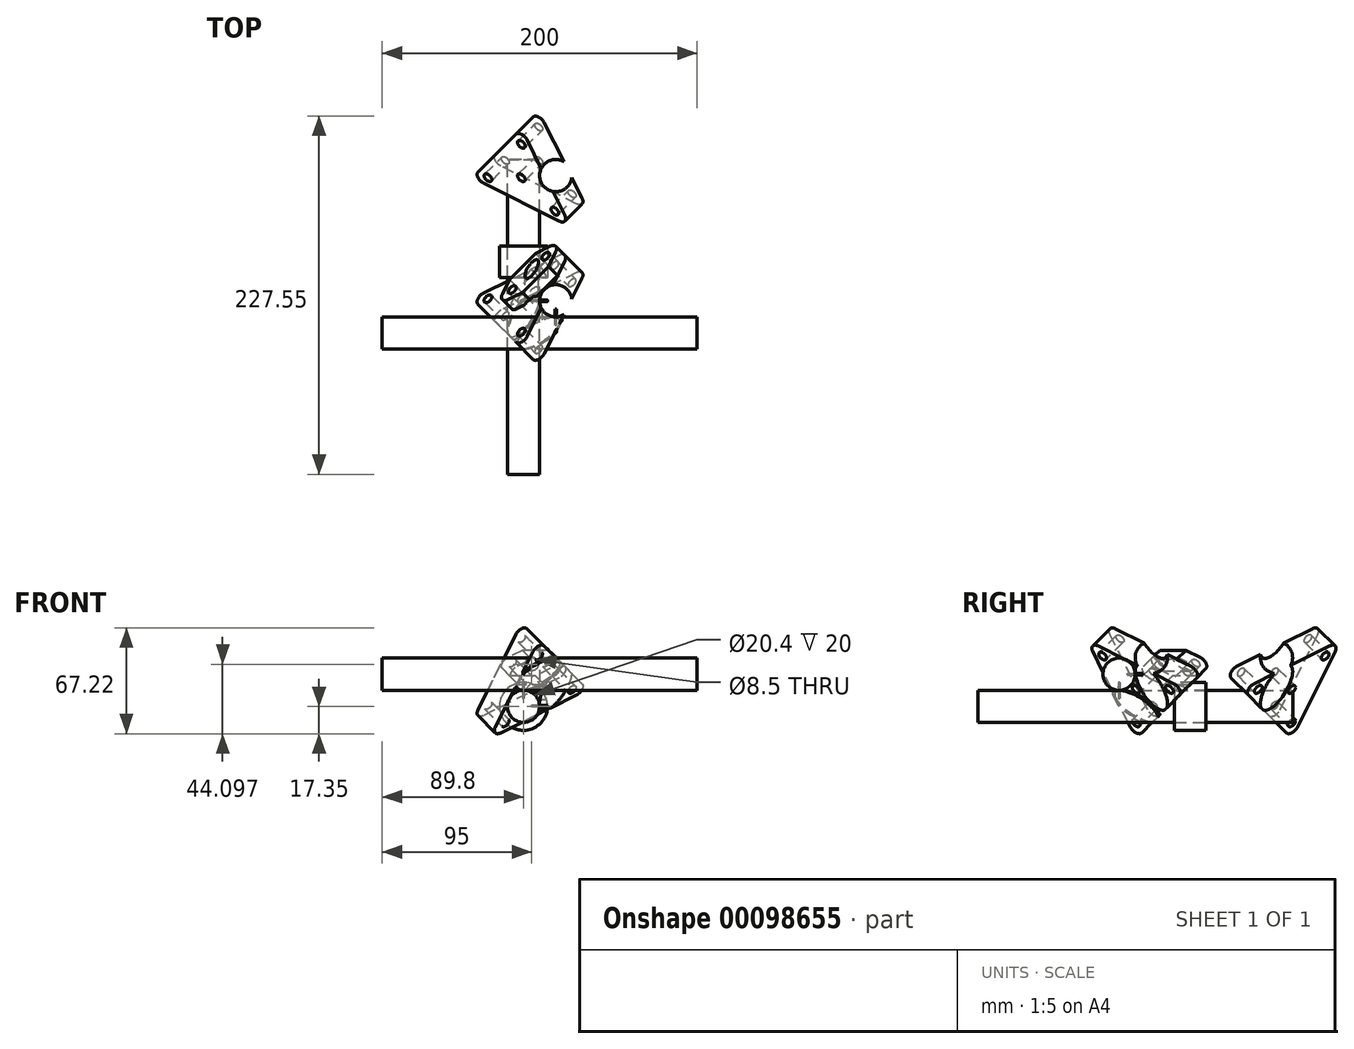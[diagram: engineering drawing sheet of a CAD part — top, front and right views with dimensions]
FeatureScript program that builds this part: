
annotation { "Feature Type Name" : "Feature", "Feature Type Description" : "" }
export const myFeature = defineFeature(function(context is Context, id is Id, definition is map)
    precondition{}
    {
        {
            var Q0;
            Q0=qCreatedBy(makeId("Top.planeOp"),FACE);
            var sketch = newSketch(context, id + "F0", { "sketchPlane" : qUnion([Q0])});
            skCircle(sketch, "E0", {"center": v(10.25, 10.25) * mm, "radius": 10.25 * mm});
            skLineSegment(sketch, "E1", {"start": v(3, 3) * mm, "end": v(14.79, -8.78) * mm, "construction": true});
            skLineSegment(sketch, "E2", {"start": v(30.79, 4.2) * mm, "end": v(17.5, 17.5) * mm, "construction": true});
            skLineSegment(sketch, "E3", {"start": v(0, 0) * mm, "end": v(17.5, 17.5) * mm, "construction": true});
            skLineSegment(sketch, "E4", {"start": v(14.79, -8.78) * mm, "end": v(30.79, 4.2) * mm, "construction": true});
            skSolve(sketch);
        }
        {
            var Q0;
            Q0=qSketchRegion(id+"F0",true);
            extrude(context, id + "F1", {"entities" : qUnion([Q0]), "endBound" : BoundingType.SYMMETRIC, "depth" : 200 * mm});
        }
        {
            var Q0;
            Q0=qCreatedBy(makeId("Right.planeOp"),FACE);
            var sketch = newSketch(context, id + "F2", { "sketchPlane" : qUnion([Q0])});
            skCircle(sketch, "E5", {"center": v(-10.25, 10.25) * mm, "radius": 10.25 * mm});
            skLineSegment(sketch, "E6", {"start": v(0, 0) * mm, "end": v(-17.5, 17.5) * mm, "construction": true});
            skLineSegment(sketch, "E7", {"start": v(-3, 3) * mm, "end": v(-20.36, -14.35) * mm, "construction": true});
            skLineSegment(sketch, "E8", {"start": v(-20.36, -14.35) * mm, "end": v(-34.85, 0.14) * mm, "construction": true});
            skLineSegment(sketch, "E9", {"start": v(-34.85, 0.14) * mm, "end": v(-17.5, 17.5) * mm, "construction": true});
            skSolve(sketch);
        }
        {
            var Q0;
            Q0=qSketchRegion(id+"F2",true);
            extrude(context, id + "F3", {"entities" : qUnion([Q0]), "endBound" : BoundingType.SYMMETRIC, "depth" : 200 * mm});
        }
        {
            var Q0;
            Q0=qCreatedBy(makeId("Front.planeOp"),FACE);
            var sketch = newSketch(context, id + "F4", { "sketchPlane" : qUnion([Q0])});
            skCircle(sketch, "E10", {"center": v(-10.2, -10.2) * mm, "radius": 10.2 * mm});
            skLineSegment(sketch, "E11", {"start": v(0, 0) * mm, "end": v(-17.41, -17.41) * mm, "construction": true});
            skLineSegment(sketch, "E12", {"start": v(-2.99, -2.99) * mm, "end": v(15.73, -21.7) * mm, "construction": true});
            skLineSegment(sketch, "E13", {"start": v(15.73, -21.7) * mm, "end": v(1.3, -36.13) * mm, "construction": true});
            skLineSegment(sketch, "E14", {"start": v(1.3, -36.13) * mm, "end": v(-17.41, -17.41) * mm, "construction": true});
            skSolve(sketch);
        }
        {
            var Q0;
            Q0=qSketchRegion(id+"F4",true);
            extrude(context, id + "F5", {"entities" : qUnion([Q0]), "endBound" : BoundingType.SYMMETRIC, "depth" : 200 * mm});
        }
        {
            var Q0;
            Q0=sQuery(id+"F2.wireOp",VERTEX,"E5.center");
            var Q1;
            Q1=sQuery(id+"F4.wireOp",VERTEX,"E10.center");
            var Q2;
            Q2=sQuery(id+"F0.wireOp",VERTEX,"E0.center");
            cPlane(context, id + "F6", {"entities" : qUnion([Q0, Q1, Q2]), "cplaneType" : CPlaneType.THREE_POINT, "offset" : 150 * mm, "width" : 150 * mm, "height" : 150 * mm});
        }
        {
            var Q0;
            Q0=qCreatedBy(makeId("Top.planeOp"),FACE);
            var sketch = newSketch(context, id + "F7", { "sketchPlane" : qUnion([Q0])});
            skLineSegment(sketch, "E15", {"start": v(-20.4, -100) * mm, "end": v(-20.4, 100) * mm});
            skLineSegment(sketch, "E16", {"start": v(0, 100) * mm, "end": v(0, -100) * mm});
            skLineSegment(sketch, "E17", {"start": v(100, -20.5) * mm, "end": v(-100, -20.5) * mm});
            skLineSegment(sketch, "E18", {"start": v(-100, 0) * mm, "end": v(100, 0) * mm});
            skLineSegment(sketch, "E19", {"start": v(-20.4, -20.5) * mm, "end": v(0, 0) * mm, "construction": true});
            skCircle(sketch, "E20", {"center": v(-10.2, -10.25) * mm, "radius": 0.5 * mm});
            skSolve(sketch);
        }
        {
            var Q0;
            Q0=makeQuery(id+"F7.imprint","IMPRINT",FACE,{"disambiguationData":[TD([[makeQuery(id+"F7.imprint","IMPRINT",EDGE,{"derivedFrom":sQuery(id+"F7.wireOp",EDGE,"E20")}),1.0]])]});
            extrude(context, id + "F8", {"entities" : qUnion([Q0]), "endBound" : BoundingType.SYMMETRIC, "depth" : 10 * mm});
        }
        {
            var Q0;
            Q0=qCreatedBy(makeId("Right.planeOp"),FACE);
            var sketch = newSketch(context, id + "F9", { "sketchPlane" : qUnion([Q0])});
            skLineSegment(sketch, "E21", {"start": v(100, -20.4) * mm, "end": v(-100, -20.4) * mm});
            skLineSegment(sketch, "E22", {"start": v(-100, 0) * mm, "end": v(100, 0) * mm});
            skLineSegment(sketch, "E23", {"start": v(20.5, 100) * mm, "end": v(20.5, -100) * mm});
            skLineSegment(sketch, "E24", {"start": v(0, -100) * mm, "end": v(0, 100) * mm});
            skLineSegment(sketch, "E25", {"start": v(20.5, -20.4) * mm, "end": v(0, 0) * mm, "construction": true});
            skCircle(sketch, "E26", {"center": v(10.25, -10.2) * mm, "radius": 0.5 * mm});
            skSolve(sketch);
        }
        {
            var Q0;
            Q0=makeQuery(id+"F9.imprint","IMPRINT",FACE,{"disambiguationData":[TD([[makeQuery(id+"F9.imprint","IMPRINT",EDGE,{"derivedFrom":sQuery(id+"F9.wireOp",EDGE,"E26")}),1.0]])]});
            extrude(context, id + "F10", {"entities" : qUnion([Q0]), "endBound" : BoundingType.SYMMETRIC, "depth" : 10 * mm});
        }
        {
            var Q0;
            Q0=qCreatedBy(makeId("Front.planeOp"),FACE);
            var sketch = newSketch(context, id + "F11", { "sketchPlane" : qUnion([Q0])});
            skLineSegment(sketch, "E27", {"start": v(0, -100) * mm, "end": v(0, 100) * mm});
            skLineSegment(sketch, "E28", {"start": v(20.5, 100) * mm, "end": v(20.5, -100) * mm});
            skLineSegment(sketch, "E29", {"start": v(-100, 20.5) * mm, "end": v(100, 20.5) * mm});
            skLineSegment(sketch, "E30", {"start": v(100, 0) * mm, "end": v(-100, 0) * mm});
            skLineSegment(sketch, "E31", {"start": v(0, 0) * mm, "end": v(20.5, 20.5) * mm, "construction": true});
            skCircle(sketch, "E32", {"center": v(10.25, 10.25) * mm, "radius": 0.5 * mm});
            skSolve(sketch);
        }
        {
            var Q0;
            Q0=makeQuery(id+"F11.imprint","IMPRINT",FACE,{"disambiguationData":[TD([[makeQuery(id+"F11.imprint","IMPRINT",EDGE,{"derivedFrom":sQuery(id+"F11.wireOp",EDGE,"E32")}),1.0]])]});
            extrude(context, id + "F12", {"entities" : qUnion([Q0]), "endBound" : BoundingType.SYMMETRIC, "depth" : 10 * mm});
        }
        {
            var Q0;
            Q0=qCreatedBy(id+"F6.planeOp",FACE);
            var sketch = newSketch(context, id + "F13", { "sketchPlane" : qUnion([Q0])});
            skLineSegment(sketch, "E33", {"start": v(0, 44) * mm, "end": v(0, -22) * mm, "construction": true});
            skLineSegment(sketch, "E34", {"start": v(0, 44) * mm, "end": v(-38.1, -22) * mm});
            skLineSegment(sketch, "E35", {"start": v(-38.1, -22) * mm, "end": v(38.1, -22) * mm});
            skLineSegment(sketch, "E36", {"start": v(38.1, -22) * mm, "end": v(0, 44) * mm});
            skLineSegment(sketch, "E37", {"start": v(-38.1, -22) * mm, "end": v(19.05, 11) * mm, "construction": true});
            skLineSegment(sketch, "E38", {"start": v(38.1, -22) * mm, "end": v(-19.05, 11) * mm, "construction": true});
            skCircle(sketch, "E39", {"center": v(0, 0) * mm, "radius": 3.05 * mm});
            skCircle(sketch, "E40", {"center": v(0, 30) * mm, "radius": 3.05 * mm});
            skCircle(sketch, "E41", {"center": v(-25.98, -15) * mm, "radius": 3.05 * mm});
            skCircle(sketch, "E42", {"center": v(25.98, -15) * mm, "radius": 3.05 * mm});
            skSolve(sketch);
        }
        {
            var Q0;
            Q0=qSketchRegion(id+"F13",true);
            extrude(context, id + "F14", {"entities" : qUnion([Q0]), "depth" : 20 * mm});
        }
        {
            var Q0;
            Q0=makeQuery(id+"F1.opExtrude","SWEPT_BODY",BODY,{"disambiguationData":[OSD([sQuery(id+"F0.wireOp",EDGE,"E0")])]});
            var Q1;
            Q1=makeQuery(id+"F14.opExtrude","SWEPT_BODY",BODY,{"disambiguationData":[OSD([sQuery(id+"F13.wireOp",EDGE,"E34"),sQuery(id+"F13.wireOp",EDGE,"E35"),sQuery(id+"F13.wireOp",EDGE,"E36"),sQuery(id+"F13.wireOp",EDGE,"E39"),sQuery(id+"F13.wireOp",EDGE,"E40"),sQuery(id+"F13.wireOp",EDGE,"E41"),sQuery(id+"F13.wireOp",EDGE,"E42")])]});
            booleanBodies(context, id + "F15", {"operationType" : BooleanOperationType.SUBTRACTION, "tools" : qUnion([Q0]), "targets" : qUnion([Q1])});
        }
        {
            var Q0;
            Q0=makeQuery(id+"F14.opExtrude","SWEPT_EDGE",EDGE,{"disambiguationData":[OSD([sQuery(id+"F13.wireOp",EDGE,"E34"),sQuery(id+"F13.wireOp",EDGE,"E36")])]});
            var Q1;
            Q1=makeQuery(id+"F14.opExtrude","SWEPT_EDGE",EDGE,{"disambiguationData":[OSD([sQuery(id+"F13.wireOp",EDGE,"E35"),sQuery(id+"F13.wireOp",EDGE,"E36")])]});
            var Q2;
            Q2=makeQuery(id+"F14.opExtrude","SWEPT_EDGE",EDGE,{"disambiguationData":[OSD([sQuery(id+"F13.wireOp",EDGE,"E34"),sQuery(id+"F13.wireOp",EDGE,"E35")])]});
            fillet(context, id + "F16", {"entities" : qUnion([Q0, Q1, Q2]), "radius" : 5 * mm, "tangentPropagation" : true, "allowEdgeOverflow" : false});
        }
        {
            var Q0;
            Q0=makeQuery(id+"F13.imprint","IMPRINT",FACE,{"disambiguationData":[TD([[makeQuery(id+"F13.imprint","IMPRINT",EDGE,{"derivedFrom":sQuery(id+"F13.wireOp",EDGE,"E34")}),1.0]])]});
            extrude(context, id + "F17", {"entities" : qUnion([Q0]), "operationType" : NewBodyOperationType.REMOVE, "depth" : 1 * mm});
        }
        {
            var Q0;
            Q0=makeQuery(id+"F14.opExtrude","SWEPT_BODY",BODY,{"disambiguationData":[OSD([sQuery(id+"F13.wireOp",EDGE,"E34"),sQuery(id+"F13.wireOp",EDGE,"E35"),sQuery(id+"F13.wireOp",EDGE,"E36"),sQuery(id+"F13.wireOp",EDGE,"E39"),sQuery(id+"F13.wireOp",EDGE,"E40"),sQuery(id+"F13.wireOp",EDGE,"E41"),sQuery(id+"F13.wireOp",EDGE,"E42")])]});
            var Q1;
            Q1=qCreatedBy(makeId("Front.planeOp"),FACE);
            mirror(context, id + "F18", {"entities" : qUnion([Q0]), "mirrorPlane" : qUnion([Q1])});
        }
        {
            var Q0;
            Q0=makeQuery(id+"F18.opPattern","COPY",BODY,{"derivedFrom":makeQuery(id+"F14.opExtrude","SWEPT_BODY",BODY,{"disambiguationData":[OSD([sQuery(id+"F13.wireOp",EDGE,"E34"),sQuery(id+"F13.wireOp",EDGE,"E35"),sQuery(id+"F13.wireOp",EDGE,"E36"),sQuery(id+"F13.wireOp",EDGE,"E39"),sQuery(id+"F13.wireOp",EDGE,"E40"),sQuery(id+"F13.wireOp",EDGE,"E41"),sQuery(id+"F13.wireOp",EDGE,"E42")])]}),"instanceName":"1"});
            transform(context, id + "F19", {"entities" : qUnion([Q0]), "transformType" : TransformType.TRANSLATION_3D, "dx" : 0 * mm, "dy" : 100 * mm, "dz" : 0 * mm, "makeCopy" : false});
        }
        {
            var Q0;
            Q0=qCreatedBy(makeId("Front.planeOp"),FACE);
            cPlane(context, id + "F20", {"entities" : qUnion([Q0]), "cplaneType" : CPlaneType.OFFSET, "offset" : 25 * mm, "oppositeDirection" : true, "width" : 150 * mm, "height" : 150 * mm});
        }
        {
            var Q0;
            Q0=qCreatedBy(id+"F20.planeOp",FACE);
            var sketch = newSketch(context, id + "F21", { "sketchPlane" : qUnion([Q0])});
            skArc(sketch, "E43.0", {"start": v(-5.66, -1.07) * mm, "mid": v(-14.76, -1.08) * mm, "end": v(-20.23, -8.35) * mm});
            skArc(sketch, "E44", {"start": v(-20.23, -8.35) * mm, "mid": v(-5.64, -19.32) * mm, "end": v(-5.66, -1.07) * mm});
            skCircle(sketch, "E45", {"center": v(-10.2, -10.2) * mm, "radius": 15.2 * mm});
            skSolve(sketch);
        }
        {
            var Q0;
            Q0 = qSketchRegion(id + "F21", true);
            extrude(context, id + "F22", {"entities" : qUnion([Q0]), "oppositeDirection" : true, "depth" : 20 * mm});
        }
        {
            var Q0;
            Q0=makeQuery(id+"F14.opExtrude","SWEPT_BODY",BODY,{"disambiguationData":[OSD([sQuery(id+"F13.wireOp",EDGE,"E34"),sQuery(id+"F13.wireOp",EDGE,"E35"),sQuery(id+"F13.wireOp",EDGE,"E36"),sQuery(id+"F13.wireOp",EDGE,"E39"),sQuery(id+"F13.wireOp",EDGE,"E40"),sQuery(id+"F13.wireOp",EDGE,"E41"),sQuery(id+"F13.wireOp",EDGE,"E42")])]});
            var Q1;
            Q1=makeQuery(id+"F22.opExtrude","SWEPT_BODY",BODY,{"disambiguationData":[OSD([sQuery(id+"F21.wireOp",EDGE,"E43.0"),sQuery(id+"F21.wireOp",EDGE,"E44"),sQuery(id+"F21.wireOp",EDGE,"E45")])]});
            booleanBodies(context, id + "F23", {"operationType" : BooleanOperationType.SUBTRACTION, "tools" : qUnion([Q0]), "targets" : qUnion([Q1]), "keepTools" : true});
        }
        {
            var Q0;
            Q0=makeQuery(id+"F14.opExtrude","CAP_FACE",FACE,{"disambiguationData":[OSD([sQuery(id+"F13.wireOp",EDGE,"E34"),sQuery(id+"F13.wireOp",EDGE,"E35"),sQuery(id+"F13.wireOp",EDGE,"E36"),sQuery(id+"F13.wireOp",EDGE,"E39"),sQuery(id+"F13.wireOp",EDGE,"E40"),sQuery(id+"F13.wireOp",EDGE,"E41"),sQuery(id+"F13.wireOp",EDGE,"E42")])],"isStart":false});
            var sketch = newSketch(context, id + "F24", { "sketchPlane" : qUnion([Q0])});
            skLineSegment(sketch, "E46", {"start": v(-25.98, -15) * mm, "end": v(0, 0) * mm, "construction": true});
            skPoint(sketch, "E47", {"position": v(-13, -7.5) * mm});
            skCircle(sketch, "E48.0", {"center": v(-25.98, -15) * mm, "radius": 3.05 * mm});
            skCircle(sketch, "E49.0", {"center": v(0, 0) * mm, "radius": 3.05 * mm});
            skLineSegment(sketch, "E50", {"start": v(-18.1, -22) * mm, "end": v(2.12, -10.32) * mm});
            skLineSegment(sketch, "E51", {"start": v(-25.98, -15) * mm, "end": v(-31.22, -18.03) * mm, "construction": true});
            skLineSegment(sketch, "E52", {"start": v(0, 0) * mm, "end": v(5.24, 3.03) * mm, "construction": true});
            skLineSegment(sketch, "E53.MirrorCS", {"start": v(-28.1, -4.68) * mm, "end": v(-7.88, 7) * mm});
            skArc(sketch, "E54.0", {"start": v(-33.77, -14.5) * mm, "mid": v(-33.77, -19.5) * mm, "end": v(-29.44, -22) * mm});
            skLineSegment(sketch, "E55", {"start": v(-13, -7.5) * mm, "end": v(-10.48, -11.84) * mm, "construction": true});
            skArc(sketch, "E56.MirrorCS", {"start": v(3.46, 7) * mm, "mid": v(7.8, 4.5) * mm, "end": v(7.8, -0.5) * mm});
            skLineSegment(sketch, "E57.0", {"start": v(-29.44, -22) * mm, "end": v(-18.1, -22) * mm});
            skLineSegment(sketch, "E58.0", {"start": v(-28.1, -4.68) * mm, "end": v(-33.77, -14.5) * mm});
            skPoint(sketch, "E59.orphan", {"position": v(-7.2, -22) * mm});
            skPoint(sketch, "E60.orphan", {"position": v(-24.43, 1.68) * mm});
            skLineSegment(sketch, "E61.MirrorCS", {"start": v(7.8, -0.5) * mm, "end": v(2.12, -10.32) * mm});
            skLineSegment(sketch, "E62.MirrorCS", {"start": v(-7.88, 7) * mm, "end": v(3.46, 7) * mm});
            skSolve(sketch);
        }
        {
            var Q0;
            Q0=qCreatedBy(makeId("Front.planeOp"),FACE);
            var Q1;
            Q1=sQuery(id+"F24.wireOp",VERTEX,"E47");
            cPlane(context, id + "F25", {"entities" : qUnion([Q0, Q1]), "cplaneType" : CPlaneType.PLANE_POINT, "offset" : 150 * mm, "width" : 150 * mm, "height" : 150 * mm});
        }
        {
            var Q0;
            Q0=qCreatedBy(id+"F25.planeOp",FACE);
            var sketch = newSketch(context, id + "F26", { "sketchPlane" : qUnion([Q0])});
            skPoint(sketch, "E63.0", {"position": v(-5, 16.55) * mm});
            skCircle(sketch, "E64", {"center": v(-5, 16.55) * mm, "radius": 4.25 * mm});
            skLineSegment(sketch, "E65.0", {"start": v(9.67, 11.55) * mm, "end": v(-11.55, 11.55) * mm});
            skSolve(sketch);
        }
        {
            var Q0;
            Q0 = qSketchRegion(id + "F26", true);
            extrude(context, id + "F27", {"entities" : qUnion([Q0]), "endBound" : BoundingType.SYMMETRIC, "depth" : 100 * mm});
        }
        {
            var Q0;
            Q0 = qSketchRegion(id + "F24", true);
            extrude(context, id + "F28", {"entities" : qUnion([Q0]), "depth" : 10 * mm});
        }
        {
            var Q0;
            Q0=makeQuery(id+"F27.opExtrude","SWEPT_BODY",BODY,{"disambiguationData":[OSD([sQuery(id+"F26.wireOp",EDGE,"E64")])]});
            var Q1;
            Q1=makeQuery(id+"F28.opExtrude","SWEPT_BODY",BODY,{"disambiguationData":[OSD([sQuery(id+"F24.wireOp",EDGE,"E48.0"),sQuery(id+"F24.wireOp",EDGE,"E49.0"),sQuery(id+"F24.wireOp",EDGE,"E50"),sQuery(id+"F24.wireOp",EDGE,"ihNIrliq-H3R9-TWVr-Ra94-1WiVHtPCXJTJ"),sQuery(id+"F24.wireOp",EDGE,"GkEZTfjY-Z4Tu-wNJf-vkro-SwpSQShDt9Xh"),sQuery(id+"F24.wireOp",EDGE,"a0bdbbf2-04d8-44a9-b0fc-b3eed8f7528f0.MirrorCS"),sQuery(id+"F24.wireOp",EDGE,"E53.MirrorCS"),sQuery(id+"F24.wireOp",EDGE,"ff99dd6a-50c1-4e35-a48b-94fbbe8486440.MirrorCS")])]});
            booleanBodies(context, id + "F29", {"operationType" : BooleanOperationType.SUBTRACTION, "tools" : qUnion([Q0]), "targets" : qUnion([Q1])});
        }
    });
